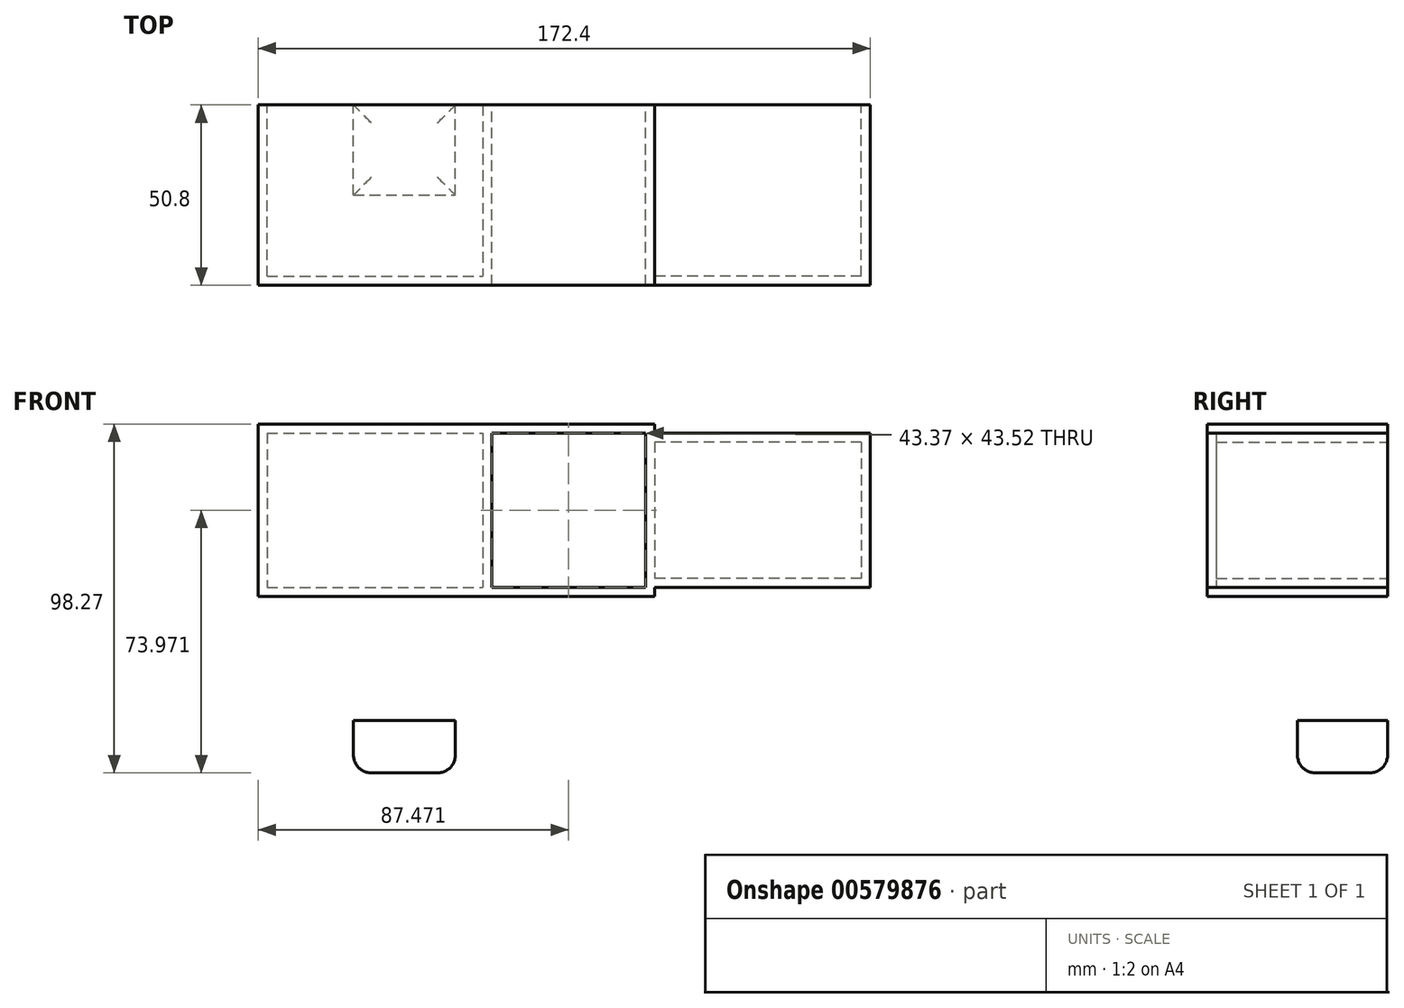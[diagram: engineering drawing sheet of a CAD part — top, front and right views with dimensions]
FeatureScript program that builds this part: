
annotation { "Feature Type Name" : "Feature", "Feature Type Description" : "" }
export const myFeature = defineFeature(function(context is Context, id is Id, definition is map)
    precondition{}
    {
        {
            var Q0;
            Q0=qCreatedBy(makeId("Front.planeOp"),FACE);
            var sketch = newSketch(context, id + "F0", { "sketchPlane" : qUnion([Q0])});
            skLineSegment(sketch, "E0.bottom", {"start": v(-73.3, 58.8) * mm, "end": v(38.4, 58.8) * mm});
            skLineSegment(sketch, "E0.top", {"start": v(-73.3, 10.2) * mm, "end": v(38.4, 10.2) * mm});
            skLineSegment(sketch, "E0.left", {"start": v(-73.3, 58.8) * mm, "end": v(-73.3, 10.2) * mm});
            skLineSegment(sketch, "E0.right", {"start": v(38.4, 58.8) * mm, "end": v(38.4, 10.2) * mm});
            skLineSegment(sketch, "E1.bottom", {"start": v(-46.45, -24.7) * mm, "end": v(-17.72, -24.7) * mm});
            skLineSegment(sketch, "E1.top", {"start": v(-46.45, -39.47) * mm, "end": v(-17.72, -39.47) * mm});
            skLineSegment(sketch, "E1.left", {"start": v(-46.45, -24.7) * mm, "end": v(-46.45, -39.47) * mm});
            skLineSegment(sketch, "E1.right", {"start": v(-17.72, -24.7) * mm, "end": v(-17.72, -39.47) * mm});
            skLineSegment(sketch, "E2.bottom", {"start": v(21.48, -17.45) * mm, "end": v(37.59, -17.45) * mm});
            skLineSegment(sketch, "E2.top", {"start": v(21.48, -49.94) * mm, "end": v(37.59, -49.94) * mm});
            skLineSegment(sketch, "E2.left", {"start": v(21.48, -17.45) * mm, "end": v(21.48, -49.94) * mm});
            skLineSegment(sketch, "E2.right", {"start": v(37.59, -17.45) * mm, "end": v(37.59, -49.94) * mm});
            skSolve(sketch);
        }
        {
            var Q0;
            Q0=makeQuery(id+"F0.imprint","IMPRINT",FACE,{"disambiguationData":[TD([[makeQuery(id+"F0.imprint","IMPRINT",EDGE,{"derivedFrom":sQuery(id+"F0.wireOp",EDGE,"E0.bottom")}),-1.0]])]});
            var Q1;
            Q1=makeQuery(id+"F0.imprint","IMPRINT",FACE,{"disambiguationData":[TD([[makeQuery(id+"F0.imprint","IMPRINT",EDGE,{"derivedFrom":sQuery(id+"F0.wireOp",EDGE,"E1.bottom")}),-1.0]])]});
            extrude(context, id + "F1", {"entities" : qUnion([Q0, Q1]), "depth" : 25.4 * mm, "offsetDistance" : 25.4 * mm});
        }
        {
            var Q0;
            Q0=makeQuery(id+"F1.opExtrude","CAP_FACE",FACE,{"disambiguationData":[OSD([sQuery(id+"F0.wireOp",EDGE,"E0.bottom"),sQuery(id+"F0.wireOp",EDGE,"E0.top"),sQuery(id+"F0.wireOp",EDGE,"E0.left"),sQuery(id+"F0.wireOp",EDGE,"E0.right")])],"isStart":false});
            var Q1;
            Q1=makeQuery(id+"F1.opExtrude","CAP_FACE",FACE,{"disambiguationData":[OSD([sQuery(id+"F0.wireOp",EDGE,"E0.bottom"),sQuery(id+"F0.wireOp",EDGE,"E0.top"),sQuery(id+"F0.wireOp",EDGE,"E0.left"),sQuery(id+"F0.wireOp",EDGE,"E0.right")])],"isStart":true});
            shell(context, id + "F2", {"entities" : qUnion([Q0, Q1]), "thickness" : 2.54 * mm});
        }
        {
            var Q0;
            Q0=makeQuery(id+"F2.opShell","OFFSET_FACE",FACE,{"disambiguationData":[OSD([sQuery(id+"F0.wireOp",EDGE,"E0.left")])]});
            var Q1;
            Q1=makeQuery(id+"F2.opShell","OFFSET_FACE",FACE,{"disambiguationData":[OSD([sQuery(id+"F0.wireOp",EDGE,"E0.right")])]});
            extrude(context, id + "F3", {"entities" : qUnion([Q0, Q1]), "operationType" : NewBodyOperationType.ADD, "depth" : 63.25 * mm, "offsetDistance" : 25.4 * mm});
        }
        {
            var Q0;
            {var subQ0=sQuery(id+"F0.wireOp",EDGE,"E0.right");var subQ1=sQuery(id+"F0.wireOp",EDGE,"E0.left");Q0=makeQuery(id+"F3.boolean.opBoolean","MERGE",FACE,{"derivedFrom":[makeQuery(id+"F1.opExtrude","CAP_FACE",FACE,{"disambiguationData":[OSD([sQuery(id+"F0.wireOp",EDGE,"E0.bottom"),sQuery(id+"F0.wireOp",EDGE,"E0.top"),subQ1,subQ0])],"isStart":false}),makeQuery(id+"F3.opExtrude","SWEPT_FACE",FACE,{"disambiguationData":[OSD([subQ1]),TDD([makeQuery(id+"F2.opShell","OFFSET_EDGE",EDGE,{"disambiguationData":[OSD([subQ1]),TDD([makeQuery(id+"F1.opExtrude","CAP_EDGE",EDGE,{"disambiguationData":[OSD([subQ1])],"isStart":false})])]})])]}),makeQuery(id+"F3.opExtrude","SWEPT_FACE",FACE,{"disambiguationData":[OSD([subQ0]),TDD([makeQuery(id+"F2.opShell","OFFSET_EDGE",EDGE,{"disambiguationData":[OSD([subQ0]),TDD([makeQuery(id+"F1.opExtrude","CAP_EDGE",EDGE,{"disambiguationData":[OSD([subQ0])],"isStart":false})])]})])]})]});}
            extrude(context, id + "F4", {"entities" : qUnion([Q0]), "operationType" : NewBodyOperationType.ADD, "depth" : 25.4 * mm, "offsetDistance" : 25.4 * mm});
        }
        {
            var Q0;
            {var subQ0=sQuery(id+"F0.wireOp",EDGE,"E0.right");var subQ1=sQuery(id+"F0.wireOp",EDGE,"E0.left");Q0=makeQuery(id+"F3.boolean.opBoolean","MERGE",FACE,{"derivedFrom":[makeQuery(id+"F1.opExtrude","CAP_FACE",FACE,{"disambiguationData":[OSD([sQuery(id+"F0.wireOp",EDGE,"E0.bottom"),sQuery(id+"F0.wireOp",EDGE,"E0.top"),subQ1,subQ0])],"isStart":true}),makeQuery(id+"F3.opExtrude","SWEPT_FACE",FACE,{"disambiguationData":[OSD([subQ1]),TDD([makeQuery(id+"F2.opShell","OFFSET_EDGE",EDGE,{"disambiguationData":[OSD([subQ1]),TDD([makeQuery(id+"F1.opExtrude","CAP_EDGE",EDGE,{"disambiguationData":[OSD([subQ1])],"isStart":true})])]})])]}),makeQuery(id+"F3.opExtrude","SWEPT_FACE",FACE,{"disambiguationData":[OSD([subQ0]),TDD([makeQuery(id+"F2.opShell","OFFSET_EDGE",EDGE,{"disambiguationData":[OSD([subQ0]),TDD([makeQuery(id+"F1.opExtrude","CAP_EDGE",EDGE,{"disambiguationData":[OSD([subQ0])],"isStart":true})])]})])]})]});}
            shell(context, id + "F5", {"entities" : qUnion([Q0]), "thickness" : 2.54 * mm});
        }
        {
            var Q0;
            Q0=makeQuery(id+"F1.opExtrude","SWEPT_FACE",FACE,{"disambiguationData":[OSD([sQuery(id+"F0.wireOp",EDGE,"E1.top")])]});
            fillet(context, id + "F6", {"entities" : qUnion([Q0]), "radius" : 5.08 * mm, "tangentPropagation" : true, "allowEdgeOverflow" : false});
        }
    });
